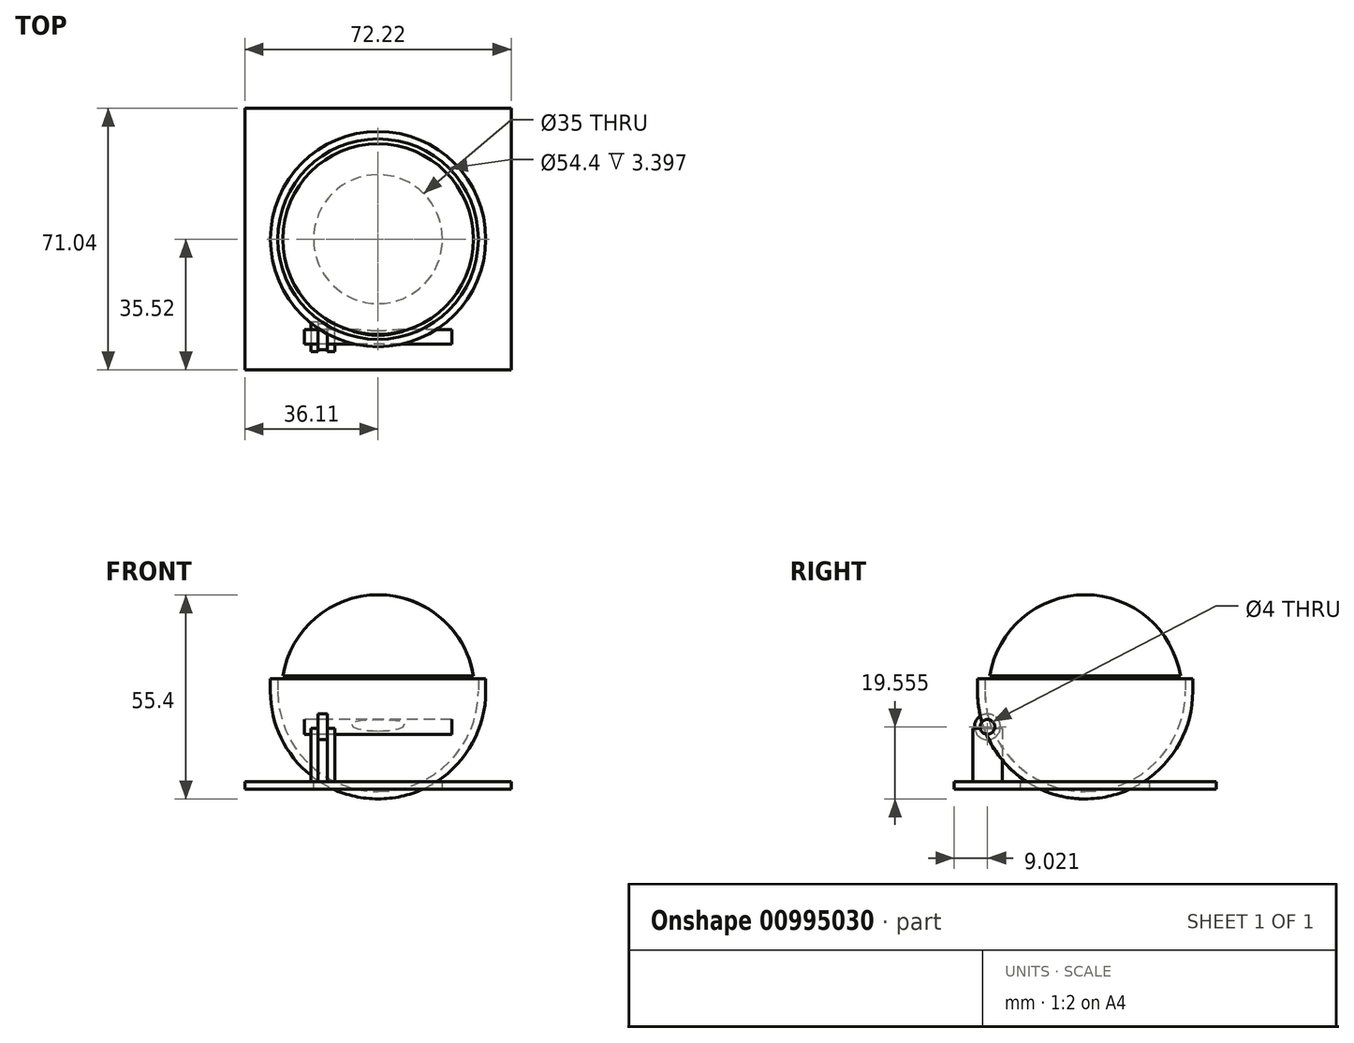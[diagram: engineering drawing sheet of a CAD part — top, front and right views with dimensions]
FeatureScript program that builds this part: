
annotation { "Feature Type Name" : "Feature", "Feature Type Description" : "" }
export const myFeature = defineFeature(function(context is Context, id is Id, definition is map)
    precondition{}
    {
        {
            var Q0;
            Q0=qCreatedBy(makeId("Front.planeOp"),FACE);
            var sketch = newSketch(context, id + "F0", { "sketchPlane" : qUnion([Q0])});
            skArc(sketch, "E0", {"start": v(0, -26.2) * mm, "mid": v(26.2, 0) * mm, "end": v(0, 26.2) * mm});
            skLineSegment(sketch, "E1", {"start": v(0, 26.2) * mm, "end": v(0, -26.2) * mm});
            skSolve(sketch);
        }
        {
            var Q0;
            Q0=qSketchRegion(id+"F0",true);
            var Q1;
            Q1=sQuery(id+"F0.wireOp",EDGE,"E1");
            revolve(context, id + "F1", {"entities" : qUnion([Q0]), "axis" : qUnion([Q1]), "revolveType" : RevolveType.FULL});
        }
        {
            var Q0;
            Q0=qCreatedBy(makeId("Top.planeOp"),FACE);
            var sketch = newSketch(context, id + "F2", { "sketchPlane" : qUnion([Q0])});
            skLineSegment(sketch, "E2.bottom", {"start": v(36.1, 35.52) * mm, "end": v(-36.1, 35.52) * mm});
            skLineSegment(sketch, "E2.top", {"start": v(36.1, -35.52) * mm, "end": v(-36.1, -35.52) * mm});
            skLineSegment(sketch, "E2.left", {"start": v(36.1, 35.52) * mm, "end": v(36.1, -35.52) * mm});
            skLineSegment(sketch, "E2.right", {"start": v(-36.1, 35.52) * mm, "end": v(-36.1, -35.52) * mm});
            skPoint(sketch, "E2.middle", {"position": v(0, 0) * mm});
            skSolve(sketch);
        }
        {
            var Q0;
            Q0=qSketchRegion(id+"F2",true);
            extrude(context, id + "F3", {"entities" : qUnion([Q0]), "depth" : 2 * mm, "offsetDistance" : 25 * mm});
        }
        {
            var Q0;
            Q0=makeQuery(id+"F3.opExtrude","CAP_FACE",FACE,{"disambiguationData":[OSD([sQuery(id+"F2.wireOp",EDGE,"E2.bottom"),sQuery(id+"F2.wireOp",EDGE,"E2.top"),sQuery(id+"F2.wireOp",EDGE,"E2.left"),sQuery(id+"F2.wireOp",EDGE,"E2.right")])],"isStart":false});
            var sketch = newSketch(context, id + "F4", { "sketchPlane" : qUnion([Q0])});
            skCircle(sketch, "E3", {"center": v(0, 0) * mm, "radius": 17.5 * mm});
            skSolve(sketch);
        }
        {
            var Q0;
            Q0=qSketchRegion(id+"F4",true);
            extrude(context, id + "F5", {"entities" : qUnion([Q0]), "operationType" : NewBodyOperationType.REMOVE, "oppositeDirection" : true, "depth" : 25 * mm, "offsetDistance" : 25 * mm});
        }
        {
            var Q0;
            Q0=makeQuery(id+"F3.opExtrude","SWEPT_BODY",BODY,{"disambiguationData":[OSD([sQuery(id+"F2.wireOp",EDGE,"E2.bottom"),sQuery(id+"F2.wireOp",EDGE,"E2.top"),sQuery(id+"F2.wireOp",EDGE,"E2.left"),sQuery(id+"F2.wireOp",EDGE,"E2.right")])]});
            transform(context, id + "F6", {"entities" : qUnion([Q0]), "transformType" : TransformType.TRANSLATION_3D, "dx" : 0 * mm, "dy" : 0 * mm, "dz" : -26.5 * mm, "makeCopy" : false});
        }
        {
            var Q0;
            Q0=qCreatedBy(makeId("Right.planeOp"),FACE);
            var sketch = newSketch(context, id + "F7", { "sketchPlane" : qUnion([Q0])});
            skCircle(sketch, "E4", {"center": v(0, 0) * mm, "radius": 3.5 * mm});
            skCircle(sketch, "E5", {"center": v(0, 0) * mm, "radius": 2 * mm});
            skSolve(sketch);
        }
        {
            var Q0;
            Q0=qSketchRegion(id+"F7",true);
            extrude(context, id + "F8", {"entities" : qUnion([Q0]), "endBound" : BoundingType.SYMMETRIC, "depth" : 2.5 * mm, "offsetDistance" : 25 * mm});
        }
        {
            var Q0;
            Q0=qCreatedBy(makeId("Right.planeOp"),FACE);
            var sketch = newSketch(context, id + "F9", { "sketchPlane" : qUnion([Q0])});
            skCircle(sketch, "E6", {"center": v(0, 0) * mm, "radius": 2 * mm});
            skSolve(sketch);
        }
        {
            var Q0;
            Q0=qSketchRegion(id+"F9",true);
            extrude(context, id + "F10", {"entities" : qUnion([Q0]), "endBound" : BoundingType.SYMMETRIC, "depth" : 40 * mm, "offsetDistance" : 25 * mm});
        }
        {
            var Q0;
            Q0=qCreatedBy(makeId("Right.planeOp"),FACE);
            var sketch = newSketch(context, id + "F11", { "sketchPlane" : qUnion([Q0])});
            skCircle(sketch, "E7", {"center": v(0, 0) * mm, "radius": 26.2 * mm});
            skCircle(sketch, "E8", {"center": v(-26.5, -9.64) * mm, "radius": 2 * mm});
            skLineSegment(sketch, "E9", {"start": v(0, 0) * mm, "end": v(-26.5, -9.64) * mm});
            skLineSegment(sketch, "E10", {"start": v(0, 0) * mm, "end": v(-32.62, 0) * mm});
            skLineSegment(sketch, "E11", {"start": v(0, 0) * mm, "end": v(0, -24.39) * mm});
            skLineSegment(sketch, "E12", {"start": v(0, -24.39) * mm, "end": v(-26.5, -24.39) * mm});
            skLineSegment(sketch, "E13", {"start": v(-26.5, -24.39) * mm, "end": v(-26.5, -9.64) * mm});
            skSolve(sketch);
        }
        {
            var Q0;
            Q0=qCreatedBy(makeId("Top.planeOp"),FACE);
            var sketch = newSketch(context, id + "F12", { "sketchPlane" : qUnion([Q0])});
            skCircle(sketch, "E14", {"center": v(0, 0) * mm, "radius": 26.2 * mm});
            skSolve(sketch);
        }
        {
            var Q0;
            Q0=qCreatedBy(makeId("Top.planeOp"),FACE);
            var Q1;
            Q1=sQuery(id+"F11.wireOp",VERTEX,"E8.center");
            cPlane(context, id + "F13", {"entities" : qUnion([Q0, Q1]), "cplaneType" : CPlaneType.PLANE_POINT, "offset" : 25 * mm, "width" : 150 * mm, "height" : 150 * mm});
        }
        {
            var Q0;
            Q0=qCreatedBy(id+"F13.planeOp",FACE);
            var sketch = newSketch(context, id + "F14", { "sketchPlane" : qUnion([Q0])});
            skLineSegment(sketch, "E15", {"start": v(0, 0) * mm, "end": v(0, -31.8) * mm});
            skLineSegment(sketch, "E16", {"start": v(32.69, 0) * mm, "end": v(0, 0) * mm});
            skLineSegment(sketch, "E17", {"start": v(0, 0) * mm, "end": v(-21.28, 21.28) * mm});
            skLineSegment(sketch, "E18.bottom", {"start": v(-16.25, -23) * mm, "end": v(-13.75, -23) * mm});
            skLineSegment(sketch, "E18.top", {"start": v(-16.25, -30) * mm, "end": v(-13.75, -30) * mm});
            skLineSegment(sketch, "E18.left", {"start": v(-16.25, -23) * mm, "end": v(-16.25, -30) * mm});
            skLineSegment(sketch, "E18.right", {"start": v(-13.75, -23) * mm, "end": v(-13.75, -30) * mm});
            skLineSegment(sketch, "E19", {"start": v(-15, -23) * mm, "end": v(-15, -26.5) * mm});
            skLineSegment(sketch, "E20", {"start": v(-16.25, -26.5) * mm, "end": v(-15, -26.5) * mm});
            skLineSegment(sketch, "E21", {"start": v(-12.45, -26.5) * mm, "end": v(-4.32, -26.5) * mm});
            skSolve(sketch);
        }
        {
            var Q0;
            Q0=makeQuery(id+"F8.opExtrude","SWEPT_BODY",BODY,{"disambiguationData":[OSD([sQuery(id+"F7.wireOp",EDGE,"E4"),sQuery(id+"F7.wireOp",EDGE,"E5")])]});
            var Q1;
            Q1=makeQuery(id+"F10.opExtrude","SWEPT_BODY",BODY,{"disambiguationData":[OSD([sQuery(id+"F9.wireOp",EDGE,"E6")])]});
            var Q2;
            Q2=sQuery(id+"F11.wireOp",EDGE,"E9");
            transform(context, id + "F15", {"entities" : qUnion([Q0, Q1]), "transformType" : TransformType.TRANSLATION_ENTITY, "oppositeDirectionEntity" : false, "transformLine" : qUnion([Q2]), "makeCopy" : false});
        }
        {
            var Q0;
            Q0=makeQuery(id+"F8.opExtrude","SWEPT_BODY",BODY,{"disambiguationData":[OSD([sQuery(id+"F7.wireOp",EDGE,"E4"),sQuery(id+"F7.wireOp",EDGE,"E5")])]});
            transform(context, id + "F16", {"entities" : qUnion([Q0]), "transformType" : TransformType.TRANSLATION_3D, "dx" : -15 * mm, "dy" : 0 * mm, "dz" : 0 * mm, "makeCopy" : false});
        }
        {
            assignVariable(context, id + "F17", {"name" : "MAGNET_THICK", "anyValue" : 2.5});
        }
        {
            var Q0;
            Q0=qCreatedBy(makeId("Right.planeOp"),FACE);
            var sketch = newSketch(context, id + "F18", { "sketchPlane" : qUnion([Q0])});
            skCircle(sketch, "E22", {"center": v(0, 0) * mm, "radius": 3 * mm});
            skSolve(sketch);
        }
        {
            var Q0;
            Q0=qSketchRegion(id+"F18",true);
            extrude(context, id + "F19", {"entities" : qUnion([Q0]), "endBound" : BoundingType.SYMMETRIC, "depth" : (getVariable(context, 'MAGNET_THICK')) * mm, "offsetDistance" : 25 * mm});
        }
        {
            var Q0;
            Q0=qCreatedBy(makeId("Front.planeOp"),FACE);
            var sketch = newSketch(context, id + "F20", { "sketchPlane" : qUnion([Q0])});
            skLineSegment(sketch, "E23", {"start": v(5.1, 4) * mm, "end": v(5.1, 0) * mm});
            skLineSegment(sketch, "E24", {"start": v(5.1, 0) * mm, "end": v(2, 0) * mm});
            skLineSegment(sketch, "E25", {"start": v(2, 0) * mm, "end": v(2, 2) * mm});
            skLineSegment(sketch, "E26", {"start": v(0, 17.59) * mm, "end": v(0, 24.73) * mm, "construction": true});
            skLineSegment(sketch, "E27", {"start": v(2, 2) * mm, "end": v(3.1, 2) * mm});
            skLineSegment(sketch, "E28", {"start": v(3.1, 2) * mm, "end": v(3.1, 4) * mm});
            skLineSegment(sketch, "E29", {"start": v(3.1, 4) * mm, "end": v(5.1, 4) * mm});
            skSolve(sketch);
        }
        {
            var Q0;
            Q0=qSketchRegion(id+"F20",true);
            var Q1;
            Q1=sQuery(id+"F20.wireOp",EDGE,"E26");
            revolve(context, id + "F21", {"entities" : qUnion([Q0]), "axis" : qUnion([Q1]), "revolveType" : RevolveType.FULL});
        }
        {
            var Q0;
            Q0=qCreatedBy(makeId("Right.planeOp"),FACE);
            var sketch = newSketch(context, id + "F22", { "sketchPlane" : qUnion([Q0])});
            skLineSegment(sketch, "E30", {"start": v(0, 0) * mm, "end": v(0, -27.2) * mm});
            skArc(sketch, "E31", {"start": v(-27.2, 0) * mm, "mid": v(-19.23, -19.23) * mm, "end": v(0, -27.2) * mm});
            skLineSegment(sketch, "E32", {"start": v(-27.2, 0) * mm, "end": v(-27.2, 4.16) * mm});
            skLineSegment(sketch, "E33", {"start": v(-27.2, 4.16) * mm, "end": v(0, 4.16) * mm});
            skLineSegment(sketch, "E34", {"start": v(0, 4.16) * mm, "end": v(0, 0) * mm});
            skSolve(sketch);
        }
        {
            var Q0;
            Q0=qCreatedBy(makeId("Right.planeOp"),FACE);
            var sketch = newSketch(context, id + "F23", { "sketchPlane" : qUnion([Q0])});
            skLineSegment(sketch, "E35", {"start": v(0, 3.4) * mm, "end": v(0, -29.2) * mm});
            skLineSegment(sketch, "E36", {"start": v(0, 3.4) * mm, "end": v(-29.2, 3.4) * mm});
            skArc(sketch, "E37", {"start": v(-29.2, 0) * mm, "mid": v(-20.65, -20.65) * mm, "end": v(0, -29.2) * mm});
            skLineSegment(sketch, "E38", {"start": v(-29.2, 0) * mm, "end": v(-29.2, 3.4) * mm});
            skSolve(sketch);
        }
        {
            var Q0;
            Q0=qSketchRegion(id+"F23",true);
            var Q1;
            Q1=sQuery(id+"F23.wireOp",EDGE,"E35");
            revolve(context, id + "F24", {"entities" : qUnion([Q0]), "axis" : qUnion([Q1]), "revolveType" : RevolveType.FULL});
        }
        {
            var Q0;
            Q0=qSketchRegion(id+"F22",true);
            var Q1;
            Q1=sQuery(id+"F22.wireOp",EDGE,"E30");
            revolve(context, id + "F25", {"operationType" : NewBodyOperationType.REMOVE, "entities" : qUnion([Q0]), "axis" : qUnion([Q1]), "revolveType" : RevolveType.FULL, "oppositeDirection" : true});
        }
        {
            var Q0;
            Q0=makeQuery(id+"F3.opExtrude","CAP_FACE",FACE,{"disambiguationData":[OSD([sQuery(id+"F2.wireOp",EDGE,"E2.bottom"),sQuery(id+"F2.wireOp",EDGE,"E2.top"),sQuery(id+"F2.wireOp",EDGE,"E2.left"),sQuery(id+"F2.wireOp",EDGE,"E2.right")])],"isStart":false});
            var sketch = newSketch(context, id + "F26", { "sketchPlane" : qUnion([Q0])});
            skLineSegment(sketch, "E39.bottom", {"start": v(-18.25, -22.4) * mm, "end": v(-16.25, -22.4) * mm});
            skLineSegment(sketch, "E39.top", {"start": v(-18.25, -30.48) * mm, "end": v(-16.25, -30.48) * mm});
            skLineSegment(sketch, "E39.left", {"start": v(-18.25, -22.4) * mm, "end": v(-18.25, -30.48) * mm});
            skLineSegment(sketch, "E39.right", {"start": v(-16.25, -22.4) * mm, "end": v(-16.25, -30.48) * mm});
            skLineSegment(sketch, "E40.bottom", {"start": v(-13.75, -30.48) * mm, "end": v(-11.75, -30.48) * mm});
            skLineSegment(sketch, "E40.top", {"start": v(-13.75, -22.43) * mm, "end": v(-11.75, -22.43) * mm});
            skLineSegment(sketch, "E40.left", {"start": v(-13.75, -30.48) * mm, "end": v(-13.75, -22.43) * mm});
            skLineSegment(sketch, "E40.right", {"start": v(-11.75, -30.48) * mm, "end": v(-11.75, -22.43) * mm});
            skLineSegment(sketch, "E41", {"start": v(-16.25, -30.48) * mm, "end": v(-13.75, -30.48) * mm});
            skPoint(sketch, "E42", {"position": v(-15, -30.48) * mm});
            skSolve(sketch);
        }
        {
            var Q0;
            Q0=qSketchRegion(id+"F26",true);
            extrude(context, id + "F27", {"entities" : qUnion([Q0]), "depth" : 14.5 * mm, "offsetDistance" : 25 * mm});
        }
    });
